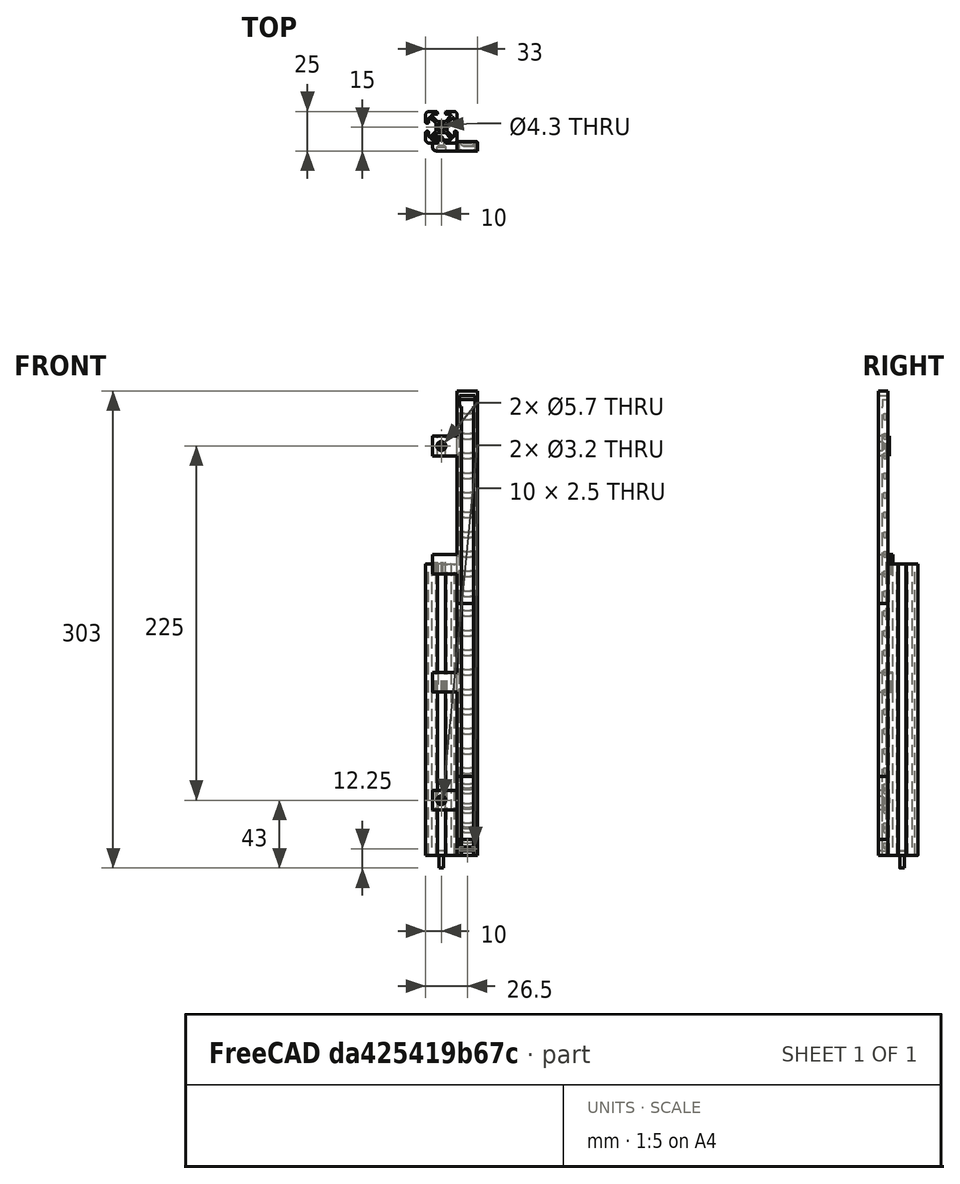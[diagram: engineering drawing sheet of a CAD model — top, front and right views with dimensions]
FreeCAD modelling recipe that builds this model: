
FCSTD DOCUMENT  (FreeCAD 0.18R)
Label: LEDstrip-Bracket-295mm
License: CreativeCommons Attribution
LicenseURL: http://creativecommons.org/licenses/by/4.0/
objects: PartDesign::Body×14, Sketcher::SketchObject×10, PartDesign::FeatureBase×8, Part::Feature×8, PartDesign::Pad×6, Part::MultiFuse×6, PartDesign::Pocket×3, Mesh::Feature×2, Spreadsheet::Sheet×1, PartDesign::Revolution×1, App::Part×1, PartDesign::Groove×1, Part::Mirroring×1
note: 69 computed .brp shape members not serialized (recipe doc carries the construction recipe); baked Part::Feature solids carry a one-line shape summary decoded from their .brp

FEATURE [Spreadsheet::Sheet] Spreadsheet  label="Par"
  cells = A1=Length of single section; B1(SectionLength)=25
FEATURE [Sketcher::SketchObject] Sketch011  label="M3x8 Profile"
  MapMode = 5
  Placement = pos=(0,0,0) rot=(1,0,0;1.5708rad)
  sketch-geometry (6):
    g0: LineSegment StartX=0 StartY=3 StartZ=0 EndX=0 EndY=-8 EndZ=0
    g1: LineSegment StartX=0 StartY=-8 StartZ=0 EndX=1.5 EndY=-8 EndZ=0
    g2: LineSegment StartX=1.5 StartY=-8 StartZ=0 EndX=1.5 EndY=0 EndZ=0
    g3: LineSegment StartX=1.5 StartY=0 StartZ=0 EndX=2.75 EndY=0 EndZ=0
    g4: LineSegment StartX=2.75 StartY=0 StartZ=0 EndX=2.75 EndY=3 EndZ=0
    g5: LineSegment StartX=2.75 StartY=3 StartZ=0 EndX=0 EndY=3 EndZ=0
  constraints (18):
    c: Coincident(g0,g1)
    c: Coincident(g1,g2)
    c: Coincident(g2,g3)
    c: Coincident(g3,g4)
    c: Coincident(g4,g5)
    c: Coincident(g0,g5)
    c: Horizontal(g5)
    c: Vertical(g0)
    c: PointOnObject(g0,g-2)
    c: Horizontal(g3)
    c: Vertical(g4)
    c: Vertical(g2)
    c: Horizontal(g1)
    c: DistanceY(g2,g2) = 8
    c: PointOnObject(g2,g-1)
    c: DistanceY(g4,g4) = 3
    c: DistanceX(g5,g5) = 2.75
    c: DistanceX(g1,g1) = 1.5
FEATURE [PartDesign::Revolution] Revolution002
  Angle = 360
  Axis = (0,-2e-16,1)
  Base = (0,0,0)
  Placement = pos=(0,0,0) rot=(1,0,0;1.5708rad)
  Profile = -> Sketch011
  ReferenceAxis = -> Sketch011 [V_Axis]
  Reversed = true
FEATURE [PartDesign::Body] Body005  label="DIN912-M3x8"
  Group = -> [Sketch011,Revolution002]
  Origin = -> Origin012
  Tip = -> Revolution002
FEATURE [App::Part] Part006  label="M3x8"
  Group = -> [Body005]
  Origin = -> Origin014
  Placement = pos=(-1e-16,-12,6.25) rot=(0.57735,0.57735,-0.57735;2.0944rad)
FEATURE [Sketcher::SketchObject] CopySketch029  label="ISP5-L20-Profile"
  MapMode = 5
  sketch-geometry (70):
    g0: LineSegment StartX=-2.5 StartY=3.5 StartZ=0 EndX=-5.91967 EndY=6.91967 EndZ=0
    g1: LineSegment StartX=-5.38934 StartY=8.2 StartZ=0 EndX=-2.85 EndY=8.2 EndZ=0
    g2: LineSegment StartX=-3.35 StartY=10 StartZ=0 EndX=-8 EndY=10 EndZ=0
    g3: LineSegment StartX=-10 StartY=8 StartZ=0 EndX=-10 EndY=3.35 EndZ=0
    g4: LineSegment StartX=-9.25 StartY=2.6 StartZ=0 EndX=-8.45 EndY=2.6 EndZ=0
    g5: LineSegment StartX=-8.2 StartY=2.85 StartZ=0 EndX=-8.2 EndY=5.38934 EndZ=0
    g6: LineSegment StartX=-6.91967 StartY=5.91967 StartZ=0 EndX=-3.5 EndY=2.5 EndZ=0
    g7: LineSegment StartX=-2.6 StartY=9.25 StartZ=0 EndX=-2.6 EndY=8.45 EndZ=0
    g8: ArcOfCircle CenterX=-8 CenterY=8 CenterZ=0 NormalX=0 NormalY=0 NormalZ=1 AngleXU=0 Radius=2 StartAngle=1.5708 EndAngle=3.14159
    g9: ArcOfCircle CenterX=-3.35 CenterY=9.25 CenterZ=0 NormalX=0 NormalY=0 NormalZ=1 AngleXU=0 Radius=0.75 StartAngle=6e-16 EndAngle=1.5708
    g10: ArcOfCircle CenterX=-9.25 CenterY=3.35 CenterZ=0 NormalX=0 NormalY=0 NormalZ=1 AngleXU=0 Radius=0.75 StartAngle=3.14159 EndAngle=4.71239
    g11: ArcOfCircle CenterX=-5.38934 CenterY=7.45 CenterZ=0 NormalX=0 NormalY=0 NormalZ=1 AngleXU=0 Radius=0.75 StartAngle=1.5708 EndAngle=3.92699
    g12: ArcOfCircle CenterX=-7.45 CenterY=5.38934 CenterZ=0 NormalX=0 NormalY=0 NormalZ=1 AngleXU=0 Radius=0.75 StartAngle=0.785398 EndAngle=3.14159
    g13: LineSegment [constr] StartX=-5.38934 StartY=7.45 StartZ=0 EndX=-7.45 EndY=5.38934 EndZ=0
    g14: ArcOfCircle CenterX=-2.85 CenterY=8.45 CenterZ=0 NormalX=0 NormalY=0 NormalZ=1 AngleXU=0 Radius=0.25 StartAngle=4.71239 EndAngle=6.28319
    g15: Circle CenterX=0 CenterY=0 CenterZ=0 NormalX=0 NormalY=0 NormalZ=1 AngleXU=0 Radius=2.15
    g16: LineSegment StartX=2.5 StartY=3.5 StartZ=0 EndX=5.91967 EndY=6.91967 EndZ=0
    g17: LineSegment StartX=3.5 StartY=-2.5 StartZ=0 EndX=6.91967 EndY=-5.91967 EndZ=0
    g18: LineSegment StartX=2.5 StartY=-3.5 StartZ=0 EndX=5.91967 EndY=-6.91967 EndZ=0
    g19: LineSegment StartX=-2.5 StartY=-3.5 StartZ=0 EndX=-5.91967 EndY=-6.91967 EndZ=0
    g20: LineSegment StartX=-3.5 StartY=-2.5 StartZ=0 EndX=-6.91967 EndY=-5.91967 EndZ=0
    g21: LineSegment StartX=3.5 StartY=2.5 StartZ=0 EndX=6.91967 EndY=5.91967 EndZ=0
    g22: ArcOfCircle CenterX=-7.45 CenterY=-5.38934 CenterZ=0 NormalX=0 NormalY=0 NormalZ=1 AngleXU=0 Radius=0.75 StartAngle=3.14159 EndAngle=5.49779
    g23: ArcOfCircle CenterX=-5.38934 CenterY=-7.45 CenterZ=0 NormalX=0 NormalY=0 NormalZ=1 AngleXU=0 Radius=0.75 StartAngle=2.35619 EndAngle=4.71239
    g24: ArcOfCircle CenterX=5.38934 CenterY=-7.45 CenterZ=0 NormalX=0 NormalY=0 NormalZ=1 AngleXU=0 Radius=0.75 StartAngle=4.71239 EndAngle=7.06858
    g25: ArcOfCircle CenterX=7.45 CenterY=-5.38934 CenterZ=0 NormalX=0 NormalY=0 NormalZ=1 AngleXU=0 Radius=0.75 StartAngle=3.92699 EndAngle=6.28319
    g26: ArcOfCircle CenterX=5.38934 CenterY=7.45 CenterZ=0 NormalX=0 NormalY=0 NormalZ=1 AngleXU=0 Radius=0.75 StartAngle=5.49779 EndAngle=7.85398
    g27: ArcOfCircle CenterX=7.45 CenterY=5.38934 CenterZ=0 NormalX=0 NormalY=0 NormalZ=1 AngleXU=0 Radius=0.75 StartAngle=6e-16 EndAngle=2.35619
    g28: LineSegment StartX=-5.38934 StartY=-8.2 StartZ=0 EndX=-2.85 EndY=-8.2 EndZ=0
    g29: LineSegment StartX=2.85 StartY=-8.2 StartZ=0 EndX=5.38934 EndY=-8.2 EndZ=0
    g30: LineSegment StartX=8.2 StartY=-5.38934 StartZ=0 EndX=8.2 EndY=-2.85 EndZ=0
    g31: LineSegment StartX=8.2 StartY=5.38934 StartZ=0 EndX=8.2 EndY=2.85 EndZ=0
    g32: LineSegment StartX=5.38934 StartY=8.2 StartZ=0 EndX=2.85 EndY=8.2 EndZ=0
    g33: LineSegment StartX=-8.2 StartY=-5.38934 StartZ=0 EndX=-8.2 EndY=-2.85 EndZ=0
    g34: ArcOfCircle CenterX=-8.45 CenterY=-2.85 CenterZ=0 NormalX=0 NormalY=0 NormalZ=1 AngleXU=0 Radius=0.25 StartAngle=7e-16 EndAngle=1.5708
    g35: ArcOfCircle CenterX=-2.85 CenterY=-8.45 CenterZ=0 NormalX=0 NormalY=0 NormalZ=1 AngleXU=0 Radius=0.25 StartAngle=1e-15 EndAngle=1.5708
    g36: ArcOfCircle CenterX=2.85 CenterY=-8.45 CenterZ=0 NormalX=0 NormalY=0 NormalZ=1 AngleXU=0 Radius=0.25 StartAngle=1.5708 EndAngle=3.14159
    g37: ArcOfCircle CenterX=8.45 CenterY=-2.85 CenterZ=0 NormalX=0 NormalY=0 NormalZ=1 AngleXU=0 Radius=0.25 StartAngle=1.5708 EndAngle=3.14159
    g38: LineSegment StartX=2.6 StartY=9.25 StartZ=0 EndX=2.6 EndY=8.45 EndZ=0
    g39: LineSegment StartX=8.45 StartY=2.6 StartZ=0 EndX=9.25 EndY=2.6 EndZ=0
    g40: LineSegment StartX=8.45 StartY=-2.6 StartZ=0 EndX=9.25 EndY=-2.6 EndZ=0
    g41: LineSegment StartX=-8.45 StartY=-2.6 StartZ=0 EndX=-9.25 EndY=-2.6 EndZ=0
    g42: LineSegment StartX=-2.6 StartY=-8.45 StartZ=0 EndX=-2.6 EndY=-9.25 EndZ=0
    g43: LineSegment StartX=2.6 StartY=-8.45 StartZ=0 EndX=2.6 EndY=-9.25 EndZ=0
    g44: ArcOfCircle CenterX=8.45 CenterY=2.85 CenterZ=0 NormalX=0 NormalY=0 NormalZ=1 AngleXU=0 Radius=0.25 StartAngle=3.14159 EndAngle=4.71239
    g45: LineSegment StartX=3.35 StartY=10 StartZ=0 EndX=8 EndY=10 EndZ=0
    g46: ArcOfCircle CenterX=8 CenterY=8 CenterZ=0 NormalX=0 NormalY=0 NormalZ=1 AngleXU=0 Radius=2 StartAngle=2e-16 EndAngle=1.5708
    g47: LineSegment StartX=10 StartY=8 StartZ=0 EndX=10 EndY=3.35 EndZ=0
    g48: ArcOfCircle CenterX=9.25 CenterY=3.35 CenterZ=0 NormalX=0 NormalY=0 NormalZ=1 AngleXU=0 Radius=0.75 StartAngle=4.71239 EndAngle=6.28319
    g49: LineSegment StartX=3.35 StartY=-10 StartZ=0 EndX=8 EndY=-10 EndZ=0
    g50: ArcOfCircle CenterX=8 CenterY=-8 CenterZ=0 NormalX=0 NormalY=0 NormalZ=1 AngleXU=0 Radius=2 StartAngle=4.71239 EndAngle=6.28319
    g51: LineSegment StartX=10 StartY=-8 StartZ=0 EndX=10 EndY=-3.35 EndZ=0
    g52: ArcOfCircle CenterX=9.25 CenterY=-3.35 CenterZ=0 NormalX=0 NormalY=0 NormalZ=1 AngleXU=0 Radius=0.75 StartAngle=1e-16 EndAngle=1.5708
    g53: LineSegment StartX=-3.35 StartY=-10 StartZ=0 EndX=-8 EndY=-10 EndZ=0
    g54: LineSegment StartX=-10 StartY=-8 StartZ=0 EndX=-10 EndY=-3.35 EndZ=0
    g55: ArcOfCircle CenterX=-9.25 CenterY=-3.35 CenterZ=0 NormalX=0 NormalY=0 NormalZ=1 AngleXU=0 Radius=0.75 StartAngle=1.5708 EndAngle=3.14159
    g56: ArcOfCircle CenterX=-3.35 CenterY=-9.25 CenterZ=0 NormalX=0 NormalY=0 NormalZ=1 AngleXU=0 Radius=0.75 StartAngle=4.71239 EndAngle=6.28319
    g57: ArcOfCircle CenterX=3.35 CenterY=-9.25 CenterZ=0 NormalX=0 NormalY=0 NormalZ=1 AngleXU=0 Radius=0.75 StartAngle=3.14159 EndAngle=4.71239
    g58: ArcOfCircle CenterX=3.35 CenterY=9.25 CenterZ=0 NormalX=0 NormalY=0 NormalZ=1 AngleXU=0 Radius=0.75 StartAngle=1.5708 EndAngle=3.14159
    g59: ArcOfCircle CenterX=-8 CenterY=-8 CenterZ=0 NormalX=0 NormalY=0 NormalZ=1 AngleXU=0 Radius=2 StartAngle=3.14159 EndAngle=4.71239
    g60: ArcOfCircle CenterX=-8.45 CenterY=2.85 CenterZ=0 NormalX=0 NormalY=0 NormalZ=1 AngleXU=0 Radius=0.25 StartAngle=4.71239 EndAngle=6.28319
    g61: ArcOfCircle CenterX=2.85 CenterY=8.45 CenterZ=0 NormalX=0 NormalY=0 NormalZ=1 AngleXU=0 Radius=0.25 StartAngle=3.14159 EndAngle=4.71239
    g62: LineSegment StartX=0 StartY=3.5 StartZ=0 EndX=2.5 EndY=3.5 EndZ=0
    g63: LineSegment StartX=0 StartY=3.5 StartZ=0 EndX=-2.5 EndY=3.5 EndZ=0
    g64: LineSegment StartX=-3.5 StartY=2.5 StartZ=0 EndX=-3.5 EndY=0 EndZ=0
    g65: LineSegment StartX=-3.5 StartY=0 StartZ=0 EndX=-3.5 EndY=-2.5 EndZ=0
    g66: LineSegment StartX=-2.5 StartY=-3.5 StartZ=0 EndX=0 EndY=-3.5 EndZ=0
    g67: LineSegment StartX=0 StartY=-3.5 StartZ=0 EndX=2.5 EndY=-3.5 EndZ=0
    g68: LineSegment StartX=3.5 StartY=-2.5 StartZ=0 EndX=3.5 EndY=0 EndZ=0
    g69: LineSegment StartX=3.5 StartY=0 StartZ=0 EndX=3.5 EndY=2.5 EndZ=0
  constraints (173):
    c: Vertical(g7)
    c: Horizontal(g1)
    c: Vertical(g5)
    c: Horizontal(g4)
    c: Coincident(g2,g9)
    c: Coincident(g9,g7)
    c: Radius(g9) = 0.75
    c: DistanceY(g1,g2) = 1.8
    c: Coincident(g3,g10)
    c: Coincident(g10,g4)
    c: Radius(g10) = 0.75
    c: Horizontal(g9,g7)
    c: Vertical(g2,g9)
    c: Coincident(g0,g11)
    c: Coincident(g11,g1)
    c: Vertical(g1,g11)
    c: Radius(g11) = 0.75
    c: Coincident(g12,g6)
    c: Coincident(g12,g5)
    c: Equal(g11,g12)
    c: Horizontal(g5,g12)
    c: Coincident(g12,g13)
    c: Coincident(g11,g13)
    c: PointOnObject(g0,g13)
    c: PointOnObject(g6,g13)
    c: Horizontal(g3,g10)
    c: Vertical(g10,g4)
    c: Horizontal(g2)
    c: Vertical(g3)
    c: Parallel(g6,g0)
    c: Tangent(g2,g8) = -1.5708
    c: Tangent(g3,g8) = -1.5708
    c: Radius(g8) = 2
    c: Perpendicular(g13,g6)
    c: Coincident(g7,g14)
    c: Coincident(g1,g14)
    c: Vertical(g14,g1)
    c: Horizontal(g14,g7)
    c: Radius(g14) = 0.25
    c: DistanceX(g3,g5) = 1.8
    c: Coincident(g15,g-1)
    c: Radius(g15) = 2.15
    c: DistanceX(g0,g16) = 5
    c: Symmetric(g16,g0,g-2)
    c: Symmetric(g21,g6,g-2)
    c: Equal(g16,g21)
    c: Parallel(g20,g19)
    c: Parallel(g18,g17)
    c: Symmetric(g6,g20,g-1)
    c: Symmetric(g0,g19,g-1)
    c: Tangent(g16,g26) = -1.5708
    c: Tangent(g21,g27) = 1.5708
    c: Tangent(g17,g25) = -1.5708
    c: Tangent(g18,g24) = 1.5708
    c: Tangent(g19,g23) = -1.5708
    c: Tangent(g20,g22) = 1.5708
    c: Horizontal(g28)
    c: Tangent(g26,g32) = -1.5708
    c: Tangent(g27,g31) = 1.5708
    c: Tangent(g25,g30) = -1.5708
    c: Tangent(g24,g29) = -1.5708
    c: Tangent(g23,g28) = -1.5708
    c: Tangent(g22,g33) = 1.5708
    c: Tangent(g30,g37) = 1.5708
    c: Tangent(g36,g29) = 1.5708
    c: Tangent(g28,g35) = 1.5708
    c: Tangent(g34,g33) = -1.5708
    c: Symmetric(g0,g16,g-2)
    c: Symmetric(g21,g17,g-1)
    c: Symmetric(g18,g19,g-2)
    c: Symmetric(g6,g20,g-1)
    c: Symmetric(g23,g1,g-1)
    c: Symmetric(g24,g26,g-1)
    c: DistanceX(g6,g21) = 7
    c: Vertical(g42)
    c: Vertical(g43)
    c: Tangent(g44,g31) = -1.5708
    c: Tangent(g44,g39) = -1.5708
    c: Tangent(g37,g40) = 1.5708
    c: Tangent(g36,g43) = -1.5708
    c: Tangent(g35,g42) = 1.5708
    c: Tangent(g41,g34) = -1.5708
    c: Symmetric(g5,g27,g-2)
    c: Symmetric(g22,g25,g-2)
    c: Vertical(g7,g35)
    c: Symmetric(g4,g41,g-1)
    c: Symmetric(g7,g38,g-2)
    c: Symmetric(g39,g40,g-1)
    c: Tangent(g45,g46) = 1.5708
    c: Tangent(g46,g47) = 1.5708
    c: Tangent(g47,g48) = 1.5708
    c: Tangent(g49,g50) = -1.5708
    c: Tangent(g50,g51) = -1.5708
    c: Tangent(g51,g52) = -1.5708
    c: Tangent(g54,g55) = 1.5708
    c: Tangent(g55,g41) = -1.5708
    c: Tangent(g40,g52) = 1.5708
    c: Tangent(g48,g39) = -1.5708
    c: Vertical(g51)
    c: Vertical(g47)
    c: Horizontal(g45)
    c: Horizontal(g49)
    c: Horizontal(g53)
    c: Tangent(g45,g58) = 1.5708
    c: Tangent(g38,g58) = -1.5708
    c: Tangent(g43,g57) = -1.5708
    c: Tangent(g49,g57) = -1.5708
    c: Tangent(g53,g56) = 1.5708
    c: Tangent(g42,g56) = 1.5708
    c: DistanceX(g3,g46) = 20
    c: Tangent(g54,g59) = 1.5708
    c: Tangent(g53,g59) = 1.5708
    c: DistanceY(g53,g2) = 20
    c: Symmetric(g54,g51,g-2)
    c: Vertical(g51,g47)
    c: Horizontal(g39)
    c: Horizontal(g40)
    c: Vertical(g54)
    c: DistanceX(g7,g38) = 5.2
    c: DistanceY(g41,g4) = 5.2
    c: DistanceY(g40,g39) = 5.2
    c: Horizontal(g2,g45)
    c: Vertical(g3,g54)
    c: Horizontal(g53,g49)
    c: Vertical(g38)
    c: Horizontal(g32)
    c: Vertical(g30)
    c: Vertical(g31)
    c: Vertical(g33)
    c: Vertical(g5,g33)
    c: Horizontal(g41)
    c: Radius(g46) = 2
    c: Radius(g50) = 2
    c: Radius(g59) = 2
    c: Radius(g56) = 0.75
    c: Symmetric(g42,g43,g-2)
    c: Radius(g35) = 0.25
    c: Radius(g44) = 0.25
    c: Radius(g34) = 0.25
    c: Radius(g37) = 0.25
    c: Tangent(g5,g60) = -1.5708
    c: Tangent(g4,g60) = -1.5708
    c: Radius(g60) = 0.25
    c: Tangent(g61,g38) = -1.5708
    c: Tangent(g32,g61) = 1.5708
    c: Radius(g61) = 0.25
    c: Radius(g36) = 0.25
    c: Horizontal(g1,g32)
    c: Coincident(g62,g63)
    c: Horizontal(g63)
    c: PointOnObject(g62,g-2)
    c: Coincident(g16,g62)
    c: Coincident(g0,g63)
    c: Coincident(g68,g69)
    c: Coincident(g66,g67)
    c: Coincident(g64,g65)
    c: Coincident(g20,g65)
    c: Coincident(g19,g66)
    c: Coincident(g18,g67)
    c: Coincident(g17,g68)
    c: Coincident(g21,g69)
    c: Coincident(g6,g64)
    c: PointOnObject(g64,g-1)
    c: PointOnObject(g68,g-1)
    c: PointOnObject(g66,g-2)
    c: Vertical(g64)
    c: Horizontal(g66)
    c: Horizontal(g67)
    c: Vertical(g69)
    c: Vertical(g68)
    c: DistanceY(g20,g6) = 5
    c: DistanceY(g19,g0) = 7
    c: Vertical(g16,g18)
FEATURE [PartDesign::Pad] Pad
  Length = 185
  Length2 = 100
  Profile = -> CopySketch029
  Type = 0
FEATURE [PartDesign::Body] Body  label="ISP5-L20"
  Group = -> [CopySketch029,Pad]
  Origin = -> Origin
  Tip = -> Pad
FEATURE [Sketcher::SketchObject] Sketch015  label="LedStrip-C-Profile"
  MapMode = 5
  Support = -> [XY_Plane031]
  sketch-geometry (13):
    g0: LineSegment StartX=10 StartY=-9 StartZ=0 EndX=10 EndY=-15 EndZ=0
    g1: LineSegment StartX=10 StartY=-15 StartZ=0 EndX=12.625 EndY=-15 EndZ=0
    g2: LineSegment StartX=12.625 StartY=-15 StartZ=0 EndX=12.625 EndY=-14.4 EndZ=0
    g3: LineSegment StartX=12.625 StartY=-14.4 StartZ=0 EndX=11.5 EndY=-14.4 EndZ=0
    g4: LineSegment StartX=11.5 StartY=-14.4 StartZ=0 EndX=11.5 EndY=-12.45 EndZ=0
    g5: LineSegment StartX=11.5 StartY=-12.45 StartZ=0 EndX=21.5 EndY=-12.45 EndZ=0
    g6: LineSegment StartX=21.5 StartY=-12.45 StartZ=0 EndX=21.5 EndY=-14.4 EndZ=0
    g7: LineSegment StartX=21.5 StartY=-14.4 StartZ=0 EndX=20.375 EndY=-14.4 EndZ=0
    g8: LineSegment StartX=20.375 StartY=-14.4 StartZ=0 EndX=20.375 EndY=-15 EndZ=0
    g9: LineSegment StartX=20.375 StartY=-15 StartZ=0 EndX=23 EndY=-15 EndZ=0
    g10: LineSegment StartX=23 StartY=-15 StartZ=0 EndX=23 EndY=-10 EndZ=0
    g11: LineSegment StartX=22 StartY=-9 StartZ=0 EndX=10 EndY=-9 EndZ=0
    g12: ArcOfCircle CenterX=22 CenterY=-10 CenterZ=0 NormalX=0 NormalY=0 NormalZ=1 AngleXU=0 Radius=1 StartAngle=0 EndAngle=1.5708
  constraints (38):
    c: Coincident(g0,g1)
    c: Coincident(g1,g2)
    c: Coincident(g2,g3)
    c: Coincident(g3,g4)
    c: Coincident(g4,g5)
    c: Coincident(g5,g6)
    c: Coincident(g6,g7)
    c: Coincident(g7,g8)
    c: Coincident(g8,g9)
    c: Horizontal(g5)
    c: Horizontal(g3)
    c: Horizontal(g7)
    c: Horizontal(g9)
    c: Horizontal(g1)
    c: Vertical(g10)
    c: Vertical(g8)
    c: Vertical(g2)
    c: Vertical(g0)
    c: Vertical(g4)
    c: DistanceX(g5,g5) = 10
    c: Vertical(g6)
    c: DistanceX(g2,g7) = 7.75
    c: Equal(g3,g7)
    c: DistanceY(g8,g8) = 0.6
    c: Horizontal(g2,g7)
    c: Horizontal(g1,g8)
    c: Horizontal(g11)
    c: DistanceY(g11,g-1) = 9
    c: DistanceY(g4,g4) = 1.95
    c: Tangent(g11,g12) = -1.5708
    c: Tangent(g10,g12) = -1.5708
    c: DistanceX(g-1,g11) = 10
    c: DistanceX(g6,g10) = 1.5
    c: Coincident(g0,g11)
    c: DistanceY(g0,g0) = 6
    c: Radius(g12) = 1
    c: Coincident(g9,g10)
    c: DistanceX(g0,g4) = 1.5
FEATURE [PartDesign::Pad] Pad009  label="LedHolderBase"
  Length = 12.5
  Length2 = 100
  Profile = -> Sketch015
  Type = 0
FEATURE [Sketcher::SketchObject] Sketch012  label="ClampFix-Profile"
  MapMode = 5
  Support = -> [XY_Plane017]
  sketch-geometry (16):
    g0: LineSegment StartX=15 StartY=3.5 StartZ=0 EndX=15 EndY=-10 EndZ=0
    g1: LineSegment StartX=15 StartY=-10 StartZ=0 EndX=9 EndY=-10 EndZ=0
    g2: LineSegment StartX=10 StartY=-8.26795 StartZ=0 EndX=10 EndY=-2.6 EndZ=0
    g3: LineSegment StartX=8.4 StartY=-1 StartZ=0 EndX=7 EndY=-1 EndZ=0
    g4: LineSegment StartX=6 StartY=5e-16 StartZ=0 EndX=6 EndY=4.5 EndZ=0
    g5: LineSegment StartX=6 StartY=4.5 StartZ=0 EndX=7.53369 EndY=4.5 EndZ=0
    g6: LineSegment StartX=8 StartY=3.5 StartZ=0 EndX=8 EndY=2.5 EndZ=0
    g7: LineSegment StartX=10 StartY=2.7 StartZ=0 EndX=10 EndY=5.5 EndZ=0
    g8: LineSegment StartX=7.53369 StartY=4.5 StartZ=0 EndX=8 EndY=3.5 EndZ=0
    g9: LineSegment StartX=8.4 StartY=-1 StartZ=0 EndX=10 EndY=-2.6 EndZ=0
    g10: LineSegment StartX=6 StartY=5e-16 StartZ=0 EndX=7 EndY=-1 EndZ=0
    g11: LineSegment StartX=8 StartY=2.5 StartZ=0 EndX=9.65 EndY=2.5 EndZ=0
    g12: LineSegment StartX=9.65 StartY=2.5 StartZ=0 EndX=10 EndY=2.7 EndZ=0
    g13: LineSegment StartX=10 StartY=5.5 StartZ=0 EndX=13 EndY=5.5 EndZ=0
    g14: ArcOfCircle CenterX=13 CenterY=3.5 CenterZ=0 NormalX=0 NormalY=0 NormalZ=1 AngleXU=0 Radius=2 StartAngle=0 EndAngle=1.5708
    g15: ArcOfCircle CenterX=8 CenterY=-8.26795 CenterZ=0 NormalX=0 NormalY=0 NormalZ=1 AngleXU=0 Radius=2 StartAngle=5.23599 EndAngle=6.28319
  constraints (47):
    c: Coincident(g0,g1)
    c: Coincident(g4,g5)
    c: Horizontal(g3)
    c: Horizontal(g5)
    c: Horizontal(g1)
    c: Vertical(g2)
    c: Vertical(g0)
    c: Vertical(g7)
    c: Vertical(g6)
    c: Vertical(g4)
    c: DistanceX(g6,g7) = 2
    c: Coincident(g5,g8)
    c: Coincident(g8,g6)
    c: DistanceX(g-1,g7) = 10
    c: DistanceY(g6,g6) = 1
    c: DistanceY(g6,g5) = 1
    c: DistanceX(g4,g6) = 2
    c: Coincident(g2,g9)
    c: Coincident(g3,g9)
    c: Coincident(g3,g10)
    c: Coincident(g4,g10)
    c: Angle(g8,g-1) = 1.13446
    c: Angle(g-1,g9) = 2.35619
    c: Parallel(g10,g9)
    c: DistanceY(g2,g-1) = 2.6
    c: DistanceY(g3,g-1) = 1
    c: DistanceX(g4,g3) = 1
    c: Coincident(g7,g12)
    c: Coincident(g11,g12)
    c: Coincident(g6,g11)
    c: DistanceY(g7) = 2.7
    c: Horizontal(g11)
    c: DistanceY(g-1,g11) = 2.5
    c: DistanceX(g11,g7) = 0.35
    c: Tangent(g13,g14) = 1.5708
    c: Coincident(g7,g13)
    c: Horizontal(g13)
    c: Tangent(g0,g14) = 1.5708
    c: Radius(g14) = 2
    c: DistanceY(g-1,g7) = 5.5
    c: DistanceY(g0,g-1) = 10
    c: Radius(g15) = 2
    c: Tangent(g2,g15) = -1.5708
    c: Coincident(g15,g1)
    c: Vertical(g7,g2)
    c: DistanceX(g1,g1) = 6
    c: DistanceX(g-1,g1) = 9
FEATURE [PartDesign::Pad] Pad006
  Length = 12.5
  Length2 = 100
  Profile = -> Sketch012
  Reversed = true
  Type = 0
FEATURE [PartDesign::Body] Body008  label="ClampFix-Part"
  Group = -> [Sketch012,Pad006]
  Origin = -> Origin017
  Placement = pos=(0,-2e-15,18.75) rot=(0.707107,-0.707107,0;3.14159rad)
  Tip = -> Pad006
FEATURE [Sketcher::SketchObject] Sketch016  label="CableStrapPath"
  AttachmentOffset = pos=(0,0,-4) rot=(0,0,1;0rad)
  Placement = pos=(0,0,6.25) rot=(1,0,0;3.14159rad)
  sketch-geometry (10):
    g0: ArcOfCircle CenterX=14.833 CenterY=8.2 CenterZ=0 NormalX=0 NormalY=0 NormalZ=1 AngleXU=0 Radius=2 StartAngle=1.5708 EndAngle=2.73008
    g1: ArcOfCircle CenterX=18.167 CenterY=8.2 CenterZ=0 NormalX=0 NormalY=0 NormalZ=1 AngleXU=0 Radius=2 StartAngle=0.411517 EndAngle=1.5708
    g2: LineSegment StartX=14.833 StartY=10.2 StartZ=0 EndX=18.167 EndY=10.2 EndZ=0
    g3: ArcOfCircle CenterX=14.25 CenterY=9.45 CenterZ=0 NormalX=0 NormalY=0 NormalZ=1 AngleXU=0 Radius=2.25 StartAngle=1.5708 EndAngle=2.46404
    g4: ArcOfCircle CenterX=18.75 CenterY=9.45 CenterZ=0 NormalX=0 NormalY=0 NormalZ=1 AngleXU=0 Radius=2.25 StartAngle=0.677555 EndAngle=1.5708
    g5: LineSegment StartX=14.25 StartY=11.7 StartZ=0 EndX=18.75 EndY=11.7 EndZ=0
    g6: LineSegment StartX=20.503 StartY=10.8605 StartZ=0 EndX=22 EndY=9 EndZ=0
    g7: LineSegment StartX=22 StartY=9 StartZ=0 EndX=20 EndY=9 EndZ=0
    g8: LineSegment StartX=12.497 StartY=10.8605 StartZ=0 EndX=11 EndY=9 EndZ=0
    g9: LineSegment StartX=11 StartY=9 StartZ=0 EndX=13 EndY=9 EndZ=0
  constraints (28):
    c: Tangent(g0,g2) = 1.5708
    c: Tangent(g1,g2) = 1.5708
    c: Horizontal(g0,g1)
    c: Horizontal(g2)
    c: Horizontal(g0,g1)
    c: Tangent(g3,g5) = 1.5708
    c: Tangent(g4,g5) = 1.5708
    c: Horizontal(g3,g4)
    c: Horizontal(g5)
    c: Horizontal(g3,g4)
    c: DistanceY(g1,g4) = 1.5
    c: Coincident(g6,g7)
    c: Coincident(g8,g9)
    c: Horizontal(g9)
    c: Horizontal(g7)
    c: Coincident(g0,g9)
    c: Coincident(g1,g7)
    c: Tangent(g4,g6) = 1.5708
    c: Tangent(g8,g3) = -1.5708
    c: DistanceX(g7,g7) = 2
    c: Equal(g9,g7)
    c: DistanceY(g1,g1) = 1.2
    c: Radius(g3) = 2.25
    c: Radius(g0) = 2
    c: DistanceX(g0,g1) = 7
    c: DistanceX(g5,g5) = 4.5
    c: DistanceY(g-1,g8) = 9
    c: DistanceX(g-1,g8) = 11
FEATURE [PartDesign::Pocket] Pocket001  label="120mmx2.5mm-CableStrapTunnel"
  BaseFeature = -> Pad009
  Length = 3.5
  Length2 = 100
  Midplane = true
  Profile = -> Sketch016
  Type = 0
FEATURE [PartDesign::Body] Body012  label="12.5mm-Segment"
  Group = -> [Sketch015,Pad009,Pocket001,Sketch016]
  Origin = -> Origin021
  Tip = -> Pocket001
FEATURE [Sketcher::SketchObject] Sketch027  label="ScrewFixProfile"
  MapMode = 5
  Support = -> [XY_Plane028]
  sketch-geometry (10):
    g0: LineSegment StartX=-3.5 StartY=-15 StartZ=0 EndX=10 EndY=-15 EndZ=0
    g1: ArcOfCircle CenterX=8.26795 CenterY=-8 CenterZ=0 NormalX=0 NormalY=0 NormalZ=1 AngleXU=0 Radius=2 StartAngle=4.71239 EndAngle=5.75959
    g2: LineSegment StartX=-5.5 StartY=-13 StartZ=0 EndX=-5.5 EndY=-10 EndZ=0
    g3: LineSegment StartX=-5.5 StartY=-10 StartZ=0 EndX=-2.5 EndY=-10 EndZ=0
    g4: LineSegment StartX=-2.5 StartY=-10 StartZ=0 EndX=-2.5 EndY=-8.2 EndZ=0
    g5: LineSegment StartX=-2.5 StartY=-8.2 StartZ=0 EndX=2.5 EndY=-8.2 EndZ=0
    g6: LineSegment StartX=2.5 StartY=-8.2 StartZ=0 EndX=2.5 EndY=-10 EndZ=0
    g7: LineSegment StartX=2.5 StartY=-10 StartZ=0 EndX=8.26795 EndY=-10 EndZ=0
    g8: ArcOfCircle CenterX=-3.5 CenterY=-13 CenterZ=0 NormalX=0 NormalY=0 NormalZ=1 AngleXU=0 Radius=2 StartAngle=3.14159 EndAngle=4.71239
    g9: LineSegment StartX=10 StartY=-9 StartZ=0 EndX=10 EndY=-15 EndZ=0
  constraints (28):
    c: Horizontal(g0)
    c: DistanceY(g0,g1) = 6
    c: DistanceY(g1,g-1) = 9
    c: Radius(g1) = 2
    c: DistanceX(g-1,g1) = 10
    c: Coincident(g2,g3)
    c: Coincident(g3,g4)
    c: Coincident(g4,g5)
    c: Coincident(g5,g6)
    c: Coincident(g6,g7)
    c: Tangent(g2,g8) = 1.5708
    c: Tangent(g0,g8) = -1.5708
    c: Tangent(g1,g7) = -1.5708
    c: Coincident(g0,g9)
    c: Coincident(g1,g9)
    c: Vertical(g9)
    c: Horizontal(g3)
    c: Vertical(g2)
    c: Vertical(g4)
    c: Vertical(g6)
    c: Horizontal(g7)
    c: DistanceX(g5,g5) = 5
    c: DistanceY(g2,g-1) = 10
    c: Horizontal(g3,g6)
    c: DistanceY(g4,g4) = 1.8
    c: DistanceX(g3,g3) = 3
    c: Symmetric(g4,g5,g-2)
    c: Radius(g8) = 2
FEATURE [PartDesign::Pad] Pad013
  Length = 12.5
  Length2 = 100
  Profile = -> Sketch027
  Type = 0
FEATURE [Sketcher::SketchObject] Sketch028  label="DIN912-M3x8-3DP-Hole-Profile002"
  Placement = pos=(0,-11,6.25) rot=(0,0,1;3.14159rad)
  sketch-geometry (6):
    g0: LineSegment StartX=0 StartY=4 StartZ=0 EndX=2.85 EndY=4 EndZ=0
    g1: LineSegment StartX=2.85 StartY=4 StartZ=0 EndX=2.85 EndY=1.5 EndZ=0
    g2: LineSegment StartX=2.85 StartY=1.5 StartZ=0 EndX=1.6 EndY=0.25 EndZ=0
    g3: LineSegment StartX=1.6 StartY=0.25 StartZ=0 EndX=1.6 EndY=-7.75 EndZ=0
    g4: LineSegment StartX=1.6 StartY=-7.75 StartZ=0 EndX=0 EndY=-7.75 EndZ=0
    g5: LineSegment StartX=0 StartY=-7.75 StartZ=0 EndX=0 EndY=4 EndZ=0
  constraints (18):
    c: Coincident(g0,g1)
    c: Coincident(g1,g2)
    c: Coincident(g2,g3)
    c: Coincident(g3,g4)
    c: Coincident(g4,g5)
    c: Coincident(g0,g5)
    c: Vertical(g5)
    c: Vertical(g1)
    c: Vertical(g3)
    c: Angle(g-1,g2) = 0.785398
    c: Horizontal(g4)
    c: DistanceX(g4,g4) = 1.6
    c: PointOnObject(g-1,g5)
    c: DistanceY(g-1,g0) = 4
    c: Horizontal(g0)
    c: DistanceY(g1,g1) = 2.5
    c: DistanceX(g0,g0) = 2.85
    c: DistanceY(g3,g2) = 8
FEATURE [PartDesign::Groove] Groove
  Angle = 360
  Axis = (0,-1,0)
  Base = (0,-11,6.25)
  BaseFeature = -> Pad013
  Profile = -> Sketch028
  ReferenceAxis = -> Sketch028 [V_Axis]
FEATURE [PartDesign::Body] Body018  label="ScrewFix-Part"
  Group = -> [Sketch027,Pad013,Sketch028,Groove]
  Origin = -> Origin028
  Placement = pos=(0,0,18.75) rot=(0,0,1;0rad)
  Tip = -> Groove
FEATURE [PartDesign::FeatureBase] Clone
  BaseFeature = -> Body012
FEATURE [PartDesign::Body] Body019  label="SF-Seg1"
  BaseFeature = -> Body012
  Group = -> [Clone]
  Origin = -> Origin029
  Tip = -> Clone
FEATURE [PartDesign::FeatureBase] Clone001
  BaseFeature = -> Body012
FEATURE [PartDesign::Body] Body020  label="CF-Seg1"
  BaseFeature = -> Body012
  Group = -> [Clone001]
  Origin = -> Origin030
  Tip = -> Clone001
FEATURE [PartDesign::Pad] Pad014  label="LedHolderBase001"
  Length = 10
  Length2 = 100
  Profile = -> Sketch015
  Type = 0
FEATURE [Sketcher::SketchObject] Sketch  label="CableViaProfile"
  MapMode = 5
  Placement = pos=(0,-12.45,0) rot=(1,0,0;1.5708rad)
  Support = -> [Pad014]
  sketch-geometry (4):
    g0: LineSegment StartX=21.5 StartY=5.5 StartZ=0 EndX=11.5 EndY=5.5 EndZ=0
    g1: LineSegment StartX=21.5 StartY=3 StartZ=0 EndX=11.5 EndY=3 EndZ=0
    g2: LineSegment StartX=11.5 StartY=5.5 StartZ=0 EndX=11.5 EndY=3 EndZ=0
    g3: LineSegment StartX=21.5 StartY=5.5 StartZ=0 EndX=21.5 EndY=3 EndZ=0
  constraints (12):
    c: Horizontal(g0)
    c: DistanceX(g0,g0) = 10
    c: Coincident(g0,g2)
    c: Coincident(g1,g2)
    c: Coincident(g0,g3)
    c: Coincident(g1,g3)
    c: Vertical(g3)
    c: Vertical(g2)
    c: Horizontal(g1)
    c: DistanceX(g-1,g1) = 11.5
    c: DistanceY(g2,g2) = 2.5
    c: DistanceY(g-1,g1) = 3
FEATURE [PartDesign::Pocket] Pocket  label="CableVIa"
  BaseFeature = -> Pad014
  Length = 5
  Length2 = 100
  Profile = -> Sketch
  Type = 0
FEATURE [Sketcher::SketchObject] Sketch029
  MapMode = 5
  Placement = pos=(0,0,0) rot=(1,0,0;3.14159rad)
  Support = -> [Pocket]
  sketch-geometry (4):
    g0: LineSegment StartX=10 StartY=15 StartZ=0 EndX=23 EndY=15 EndZ=0
    g1: LineSegment StartX=23 StartY=15 StartZ=0 EndX=23 EndY=12 EndZ=0
    g2: LineSegment StartX=23 StartY=12 StartZ=0 EndX=10 EndY=12 EndZ=0
    g3: LineSegment StartX=10 StartY=12 StartZ=0 EndX=10 EndY=15 EndZ=0
  constraints (12):
    c: Coincident(g0,g1)
    c: Coincident(g1,g2)
    c: Coincident(g2,g3)
    c: Coincident(g3,g0)
    c: Horizontal(g0)
    c: Horizontal(g2)
    c: Vertical(g1)
    c: Vertical(g3)
    c: DistanceX(g0,g0) = 13
    c: DistanceX(g-1,g0) = 10
    c: DistanceY(g3,g3) = 3
    c: DistanceY(g-1,g0) = 15
FEATURE [PartDesign::Pad] Pad015
  BaseFeature = -> Pocket
  Length = 3
  Length2 = 100
  Profile = -> Sketch029
  Reversed = true
  Type = 0
FEATURE [Sketcher::SketchObject] Sketch030
  MapMode = 5
  Placement = pos=(0,-15,0) rot=(1,0,0;1.5708rad)
  Support = -> [Pad015]
  sketch-geometry (4):
    g0: LineSegment StartX=11.5 StartY=10 StartZ=0 EndX=21.5 EndY=10 EndZ=0
    g1: LineSegment StartX=21.5 StartY=10 StartZ=0 EndX=21.5 EndY=3 EndZ=0
    g2: LineSegment StartX=21.5 StartY=3 StartZ=0 EndX=11.5 EndY=3 EndZ=0
    g3: LineSegment StartX=11.5 StartY=3 StartZ=0 EndX=11.5 EndY=10 EndZ=0
  constraints (12):
    c: Coincident(g0,g1)
    c: Coincident(g1,g2)
    c: Coincident(g2,g3)
    c: Coincident(g3,g0)
    c: Horizontal(g0)
    c: Horizontal(g2)
    c: Vertical(g1)
    c: Vertical(g3)
    c: DistanceX(g-1,g2) = 11.5
    c: DistanceX(g0,g0) = 10
    c: DistanceY(g-1,g2) = 3
    c: DistanceY(g3,g3) = 7
FEATURE [PartDesign::Pocket] Pocket002
  BaseFeature = -> Pad015
  Length = 1
  Length2 = 100
  Profile = -> Sketch030
  Type = 0
FEATURE [PartDesign::Body] Body021  label="10mm-EndBracket-Bottom"
  Group = -> [Pad014,Sketch,Pocket,Sketch029,Pad015,Sketch030,Pocket002]
  Origin = -> Origin031
  Tip = -> Pocket002
FEATURE [PartDesign::FeatureBase] Clone002
  BaseFeature = -> Body019
FEATURE [PartDesign::Body] Body022  label="SF-Seg2"
  BaseFeature = -> Body019
  Group = -> [Clone002]
  Origin = -> Origin032
  Placement = pos=(0,0,12.5) rot=(0,0,1;0rad)
  Tip = -> Clone002
FEATURE [Part::Mirroring] Part__Mirroring  label="10mm-EndBracket-Top"
  Base = (0,0,147.5)
  Normal = (0,0,1)
  Source = -> Body021
FEATURE [Part::Feature] Body012001  label="LedStripBracket-12.5mm-Segment001"
  shape: bbox 13 x 6 x 12.5 mm, 25 faces (baked)
FEATURE [Part::Feature] Body012002  label="LedStripBracket-12.5mm-Segment002"
  Placement = pos=(0,0,12.5) rot=(0,0,1;0rad)
  shape: bbox 13 x 6 x 12.5 mm, 25 faces (baked)
FEATURE [Part::MultiFuse] Fusion003  label="25mm-Segment"
  Placement = pos=(0,0,60) rot=(0,0,1;0rad)
  Shapes = -> [Body012002,Body012001]
FEATURE [Part::Feature] Fusion003001  label="25mm-Segment001"
  shape: bbox 13 x 6 x 25 mm, 48 faces (baked)
FEATURE [Part::Feature] Fusion003002  label="25mm-Segment002"
  Placement = pos=(0,0,25) rot=(0,0,1;0rad)
  shape: bbox 13 x 6 x 25 mm, 48 faces (baked)
FEATURE [Part::MultiFuse] Fusion003003  label="50mm-Segment"
  Shapes = -> [Fusion003002,Fusion003001]
FEATURE [PartDesign::FeatureBase] Clone004
  BaseFeature = -> Body012
FEATURE [PartDesign::Body] Body012004  label="SF-Seg3"
  Group = -> [Clone004]
  Origin = -> Origin034
  Placement = pos=(0,0,25) rot=(0,0,1;0rad)
  Tip = -> Clone004
FEATURE [PartDesign::FeatureBase] Clone005
  BaseFeature = -> Body012
FEATURE [PartDesign::Body] Body012005  label="SF-Seg4"
  Group = -> [Clone005]
  Origin = -> Origin035
  Placement = pos=(0,0,37.5) rot=(0,0,1;0rad)
  Tip = -> Clone005
FEATURE [Part::MultiFuse] Fusion  label="50mm-ScrewFix"
  Placement = pos=(0,0,10) rot=(0,0,1;0rad)
  Shapes = -> [Body018,Body019,Body022,Body012004,Body012005]
FEATURE [PartDesign::FeatureBase] Clone006
  BaseFeature = -> Clone001
FEATURE [PartDesign::Body] Body012006  label="CF-Seg2"
  Group = -> [Clone006]
  Origin = -> Origin036
  Placement = pos=(0,0,12.5) rot=(0,0,1;0rad)
  Tip = -> Clone006
FEATURE [PartDesign::FeatureBase] Clone007
  BaseFeature = -> Clone001
FEATURE [PartDesign::Body] Body012007  label="CF-Seg3"
  Group = -> [Clone007]
  Origin = -> Origin037
  Placement = pos=(0,0,25) rot=(0,0,1;0rad)
  Tip = -> Clone007
FEATURE [PartDesign::FeatureBase] Clone008
  BaseFeature = -> Clone001
FEATURE [PartDesign::Body] Body012008  label="CF-Seg4"
  Group = -> [Clone008]
  Origin = -> Origin038
  Placement = pos=(0,0,37.5) rot=(0,0,1;0rad)
  Tip = -> Clone008
FEATURE [Part::MultiFuse] Fusion002  label="50mm-ClampFix"
  Placement = pos=(0,0,85) rot=(0,0,1;0rad)
  Shapes = -> [Body008,Body020,Body012006,Body012007,Body012008]
FEATURE [Part::Feature] Fusion002001  label="50mm-ClampFix001"
  Placement = pos=(0,0,160) rot=(0,0,1;0rad)
  shape: bbox 28.5 x 9 x 50 mm, 111 faces (baked)
FEATURE [Part::Feature] Fusion003004  label="50mm-ScrewFix001"
  Placement = pos=(0,0,235) rot=(0,0,1;0rad)
  shape: bbox 28.5 x 6.8 x 50 mm, 108 faces (baked)
FEATURE [Part::Feature] Fusion003005  label="25mm-Segment003"
  Placement = pos=(0,0,210) rot=(0,0,1;0rad)
  shape: bbox 13 x 6 x 25 mm, 48 faces (baked)
FEATURE [Part::Feature] Fusion003005001  label="25mm-Segment004"
  Placement = pos=(0,0,135) rot=(0,0,1;0rad)
  shape: bbox 13 x 6 x 25 mm, 48 faces (baked)
FEATURE [Part::MultiFuse] Fusion003005002  label="LEDStrip-295-Part1"
  Shapes = -> [Fusion,Fusion002,Body021,Fusion003,Fusion003005001]
FEATURE [Part::MultiFuse] Fusion003005003  label="LEDStrip-295-Part2"
  Shapes = -> [Body021,Fusion003005,Fusion003004,Fusion002001,Part__Mirroring]
FEATURE [Mesh::Feature] Mesh  label="LEDStrip-295-Part1 (Meshed)"
  Placement = pos=(0,0,0) rot=(1,0,0;1.5708rad)
FEATURE [Mesh::Feature] Mesh001  label="LEDStrip-295-Part2 (Meshed)"
  Placement = pos=(-23,8.4e-15,38) rot=(1,0,0;1.5708rad)
